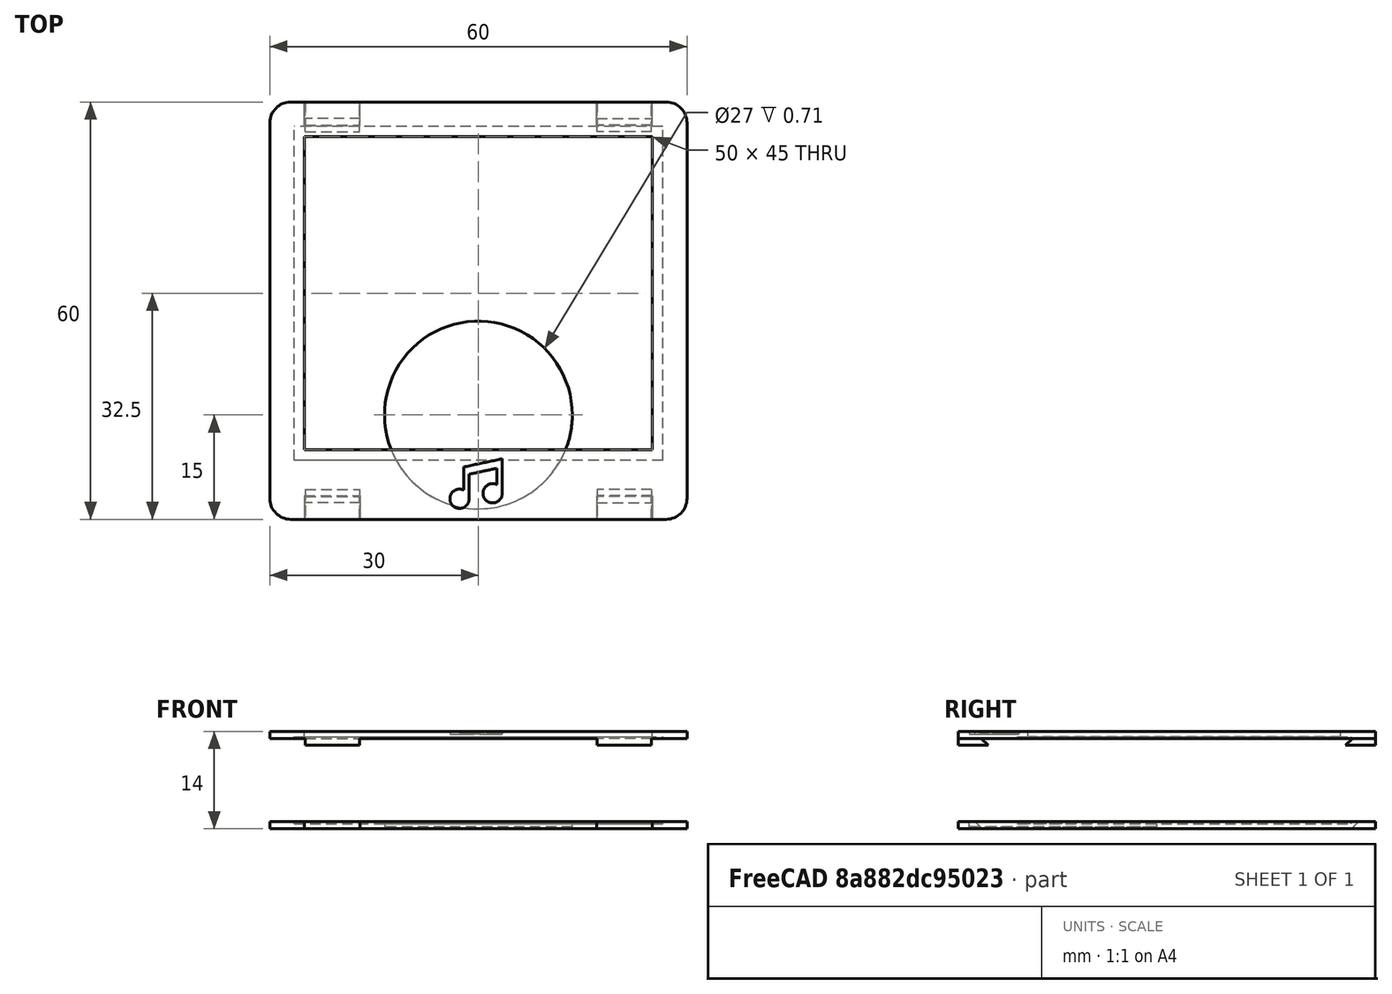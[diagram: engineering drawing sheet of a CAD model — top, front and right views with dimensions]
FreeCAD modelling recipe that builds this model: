
FCSTD DOCUMENT  (FreeCAD 1.0R39109 (Git))
Label: plastic
License: All rights reserved
LicenseURL: https://en.wikipedia.org/wiki/All_rights_reserved
objects: Part::Mirroring×7, Part::Box×6, Part::Cut×6, Part::MultiFuse×3, PartDesign::FeatureBase×2, PartDesign::Fillet×2, PartDesign::Draft×2, PartDesign::Body×2, Part::Feature×1, Part::Cylinder×1, Part::FeaturePython×1, Part::Extrusion×1
note: 44 computed .brp shape members not serialized (recipe doc carries the construction recipe); baked Part::Feature solids carry a one-line shape summary decoded from their .brp

FEATURE [Part::Feature] Path  label="Note"
  shape: bbox 5.027 x 4.763 x 2e-07 mm, 0 faces, 0 solids (baked)
FEATURE [Part::Box] Box  label="Window"
  AttacherType = Attacher::AttachEngine3D
  Height = 2
  Length = 50
  Placement = pos=(-25,-20,0.5) rot=(0,0,1;0rad)
  Width = 45
FEATURE [Part::Box] Box001  label="Frame"
  AttacherType = Attacher::AttachEngine3D
  Height = 1.01
  Length = 60
  Placement = pos=(-30,-30,0.99) rot=(0,0,1;0rad)
  Width = 60
FEATURE [Part::Cut] Cut
  Base = -> Box001
  Tool = -> Box
FEATURE [Part::Mirroring] Part__Mirroring  label="Frame (Mirror #1)"
  Base = (0,0,-5)
  Normal = (0,0,1)
  Source = -> Box001
FEATURE [Part::Cylinder] Cylinder
  Angle = 360
  AttacherType = Attacher::AttachEngine3D
  FirstAngle = 0
  Height = 2
  Placement = pos=(0,-15,-11.7) rot=(0,0,1;0rad)
  Radius = 13.5
  SecondAngle = 0
FEATURE [Part::Cut] Cut002
  Base = -> Part__Mirroring
  Tool = -> Cylinder
FEATURE [Part::Box] Box002  label="Window001"
  AttacherType = Attacher::AttachEngine3D
  Height = 2
  Length = 53
  Placement = pos=(-26.5,-21.5,-11.3) rot=(0,0,1;0rad)
  Width = 48
FEATURE [Part::Cut] Cut003  label="BackWithPictureAndTagInsets"
  Base = -> Cut002
  Tool = -> Box002
FEATURE [Part::Box] Box003  label="Cube"
  AttacherType = Attacher::AttachEngine3D
  Height = 1
  Length = 7.8
  Placement = pos=(-24.9,26.7,0) rot=(0,0,1;0rad)
  Width = 3.3
FEATURE [Part::Mirroring] Part__Mirroring001  label="Cube (Mirror #2)"
  Base = (5.96046e-08,0,0)
  Normal = (1,-1e-16,-3.57628e-07)
  Source = -> Box003
FEATURE [Part::Mirroring] Part__Mirroring002  label="Cube (Mirror #3)"
  Base = (0,0,0)
  Normal = (-4e-16,1,-3.57628e-07)
  Source = -> Box003
FEATURE [Part::Mirroring] Part__Mirroring003  label="Cube (Mirror #4)"
  Base = (0,0,0)
  Normal = (-9e-16,1,-3.57628e-07)
  Source = -> Part__Mirroring001
FEATURE [Part::MultiFuse] Fusion  label="Hooks"
  Shapes = -> [Part__Mirroring002,Part__Mirroring001,Part__Mirroring003,Box003]
FEATURE [Part::Box] Box005  label="Cube002"
  AttacherType = Attacher::AttachEngine3D
  Height = 1.1
  Length = 8
  Placement = pos=(-25,26.6,0) rot=(0,0,1;0rad)
  Width = 3.4
FEATURE [Part::Mirroring] Part__Mirroring004  label="Cube002 (Mirror #2)001"
  Base = (0,0,0)
  Normal = (1,-4e-16,-3.57628e-07)
  Source = -> Box005
FEATURE [Part::Mirroring] Part__Mirroring005  label="Cube002 (Mirror #3)001"
  Base = (0,0,0)
  Normal = (0,1,0)
  Source = -> Box005
FEATURE [Part::Mirroring] Part__Mirroring006  label="Cube002 (Mirror #4)001"
  Base = (0,0,0)
  Normal = (0,1,0)
  Source = -> Part__Mirroring004
FEATURE [Part::MultiFuse] Fusion001  label="Hooks001"
  Placement = pos=(0,0,-12) rot=(0,0,1;0rad)
  Shapes = -> [Part__Mirroring005,Part__Mirroring004,Part__Mirroring006,Box005]
FEATURE [Part::Cut] Cut006  label="BackWithHookInsets"
  Base = -> Cut003
  Tool = -> Fusion001
FEATURE [Part::MultiFuse] Fusion002  label="FrameWithHooks"
  Shapes = -> [Fusion,Cut]
FEATURE [PartDesign::FeatureBase] BaseFeature001
  BaseFeature = -> Cut006
  Suppressed = false
FEATURE [PartDesign::Fillet] Fillet001
  Base = -> BaseFeature001 [Edge1,Edge60,Edge3,Edge59]
  BaseFeature = -> BaseFeature001
  Radius = 3
  SupportTransform = false
  Suppressed = false
  UseAllEdges = false
FEATURE [PartDesign::Draft] Draft001
  Angle = 45
  Base = -> Fillet001 [Face8,Face15,Face22,Face14]
  BaseFeature = -> Fillet001
  NeutralPlane = -> Fillet001 [Face2]
  SupportTransform = false
  Suppressed = false
FEATURE [PartDesign::Body] Body001  label="Back"
  AllowCompound = false
  BaseFeature = -> Cut006
  Group = -> [BaseFeature001,Fillet001,Draft001]
  Origin = -> Origin001
  Tip = -> Draft001
FEATURE [Part::Box] Box006  label="Window002"
  AttacherType = Attacher::AttachEngine3D
  Height = 2
  Length = 53
  Placement = pos=(-26.5,-21.5,-0.8) rot=(0,0,1;0rad)
  Width = 48
FEATURE [Part::FeaturePython] Clone  label="NoteScaled"  # Draft clone (typed FeaturePython)
  AttacherType = Attacher::AttachEngine3D
  Fuse = false
  Objects = -> [Path]
  Scale = (1.5,1.5,1.5)
FEATURE [Part::Extrusion] Extrude  label="NoteExtruded"
  Base = -> Clone
  Dir = (0,0,-1)
  DirMode = 2
  FaceMakerClass = Part::FaceMakerBullseye
  FaceMakerMode = 3
  LengthFwd = 0.5
  LengthRev = 0
  Placement = pos=(-4.9,-20.1,2.1) rot=(0,0,1;0rad)
  Solid = true
  Symmetric = false
FEATURE [Part::Cut] Cut007  label="FrameWithHooksAndNote"
  Base = -> Fusion002
  Tool = -> Extrude
FEATURE [Part::Cut] Cut008  label="FrameWithHooksAndNoteAndInset"
  Base = -> Cut007
  Tool = -> Box006
FEATURE [PartDesign::FeatureBase] BaseFeature
  BaseFeature = -> Cut008
  Suppressed = false
FEATURE [PartDesign::Fillet] Fillet
  Base = -> BaseFeature [Edge40,Edge54,Edge42,Edge43]
  BaseFeature = -> BaseFeature
  Radius = 3
  SupportTransform = false
  Suppressed = false
  UseAllEdges = false
FEATURE [PartDesign::Draft] Draft
  Angle = 45
  Base = -> Fillet [Face6,Face13,Face12,Face18]
  BaseFeature = -> Fillet
  NeutralPlane = -> Fillet [Face1]
  SupportTransform = false
  Suppressed = false
FEATURE [PartDesign::Body] Body  label="Front"
  AllowCompound = false
  BaseFeature = -> Cut008
  Group = -> [BaseFeature,Fillet,Draft]
  Origin = -> Origin
  Tip = -> Draft
